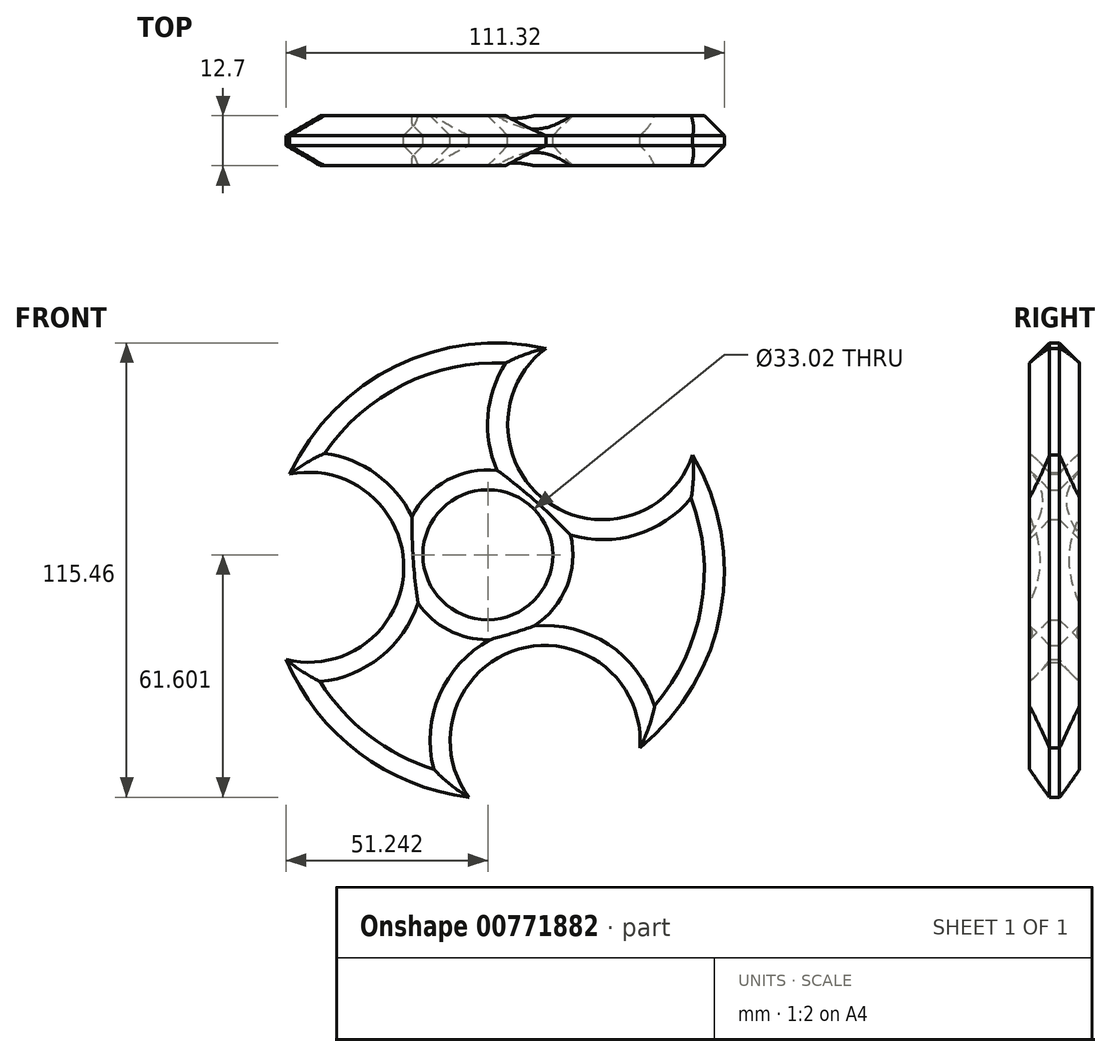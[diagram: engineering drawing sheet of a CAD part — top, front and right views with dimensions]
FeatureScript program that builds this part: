
annotation { "Feature Type Name" : "Feature", "Feature Type Description" : "" }
export const myFeature = defineFeature(function(context is Context, id is Id, definition is map)
    precondition{}
    {
        {
            var Q0;
            Q0=qCreatedBy(makeId("Front.planeOp"),FACE);
            var sketch = newSketch(context, id + "F0", { "sketchPlane" : qUnion([Q0])});
            skCircle(sketch, "E0", {"center": v(-72.8, -8.97) * mm, "radius": 57.94 * mm});
            skSolve(sketch);
        }
        {
            var Q0;
            Q0=qCreatedBy(makeId("Front.planeOp"),FACE);
            var sketch = newSketch(context, id + "F1", { "sketchPlane" : qUnion([Q0])});
            skPoint(sketch, "E1", {"position": v(-45.79, 28.15) * mm});
            skPoint(sketch, "E2", {"position": v(-120.44, -8.06) * mm});
            skPoint(sketch, "E3", {"position": v(-60.4, -52.07) * mm});
            skSolve(sketch);
        }
        {
            var Q0;
            Q0=qSketchRegion(id+"F0",true);
            extrude(context, id + "F2", {"entities" : qUnion([Q0]), "depth" : 12.7 * mm, "offsetDistance" : 25.4 * mm});
        }
        {
            var Q0;
            Q0=sQuery(id+"F1.wireOp",VERTEX,"E1");
            var Q1;
            Q1=sQuery(id+"F1.wireOp",VERTEX,"E2");
            var Q2;
            Q2=sQuery(id+"F1.wireOp",VERTEX,"E3");
            var Q3;
            Q3=makeQuery(id+"F2.opExtrude","SWEPT_BODY",BODY,{"disambiguationData":[OSD([sQuery(id+"F0.wireOp",EDGE,"E0")])]});
            hole(context, id + "F3", {"style" : HoleStyle.SIMPLE, "endStyle" : HoleEndStyle.THROUGH, "oppositeDirection" : true, "holeDiameter" : 48.26 * mm, "majorDiameter" : 6.35 * mm, "isTappedThrough" : true, "tappedDepth" : 12.7 * mm, "tapClearance" : 3, "locations" : qUnion([Q0, Q1, Q2]), "scope" : qUnion([Q3])});
        }
        {
            var Q0;
            Q0=qCreatedBy(makeId("Front.planeOp"),FACE);
            var sketch = newSketch(context, id + "F4", { "sketchPlane" : qUnion([Q0])});
            skPoint(sketch, "E4", {"position": v(-74.94, -4.89) * mm});
            skSolve(sketch);
        }
        {
            var Q0;
            Q0=sQuery(id+"F4.wireOp",VERTEX,"E4");
            var Q1;
            Q1=makeQuery(id+"F2.opExtrude","SWEPT_BODY",BODY,{"disambiguationData":[OSD([sQuery(id+"F0.wireOp",EDGE,"E0")])]});
            hole(context, id + "F5", {"style" : HoleStyle.SIMPLE, "endStyle" : HoleEndStyle.THROUGH, "oppositeDirection" : true, "holeDiameter" : 33.02 * mm, "majorDiameter" : 6.35 * mm, "isTappedThrough" : true, "tappedDepth" : 12.7 * mm, "tapClearance" : 3, "locations" : qUnion([Q0]), "scope" : qUnion([Q1])});
        }
        {
            var Q0;
            Q0=makeQuery(id+"F2.opExtrude","CAP_FACE",FACE,{"disambiguationData":[OSD([sQuery(id+"F0.wireOp",EDGE,"E0")])],"isStart":false});
            var Q1;
            Q1=makeQuery(id+"F2.opExtrude","CAP_FACE",FACE,{"disambiguationData":[OSD([sQuery(id+"F0.wireOp",EDGE,"E0")])],"isStart":true});
            chamfer(context, id + "F6", {"entities" : qUnion([Q0, Q1]), "width" : 5.08 * mm, "tangentPropagation" : true});
        }
    });
